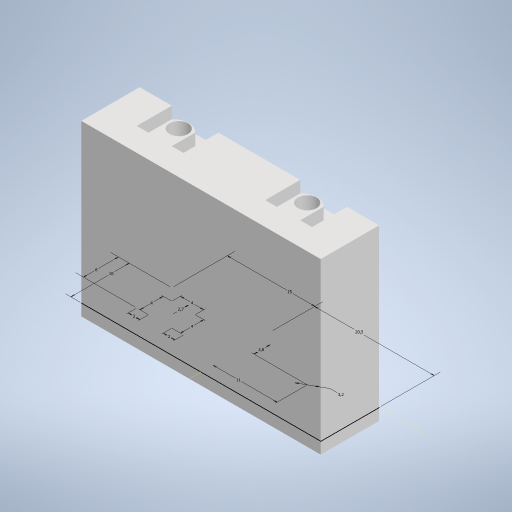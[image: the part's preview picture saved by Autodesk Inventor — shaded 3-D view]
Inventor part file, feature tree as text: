
AUTODESK INVENTOR PART (.ipt)
format: ipt  version: 2024.2 (Build 282272000, 272)  size: 267,264 bytes
history: native  units: mm
features: extrude x3, sketch x3, other x1
ambient origin geometry x8: Origin, YZ Plane, XZ Plane, XY Plane, X Axis, Y Axis, Z Axis, Center Point
bodies: Body1 (feature_tree)
feature tree (7):
  other  "Bryła1"
  extrude  "Wyciągnięcie proste1"  Depth=41.0mm
  sketch  "Szkic2"
  sketch  "Szkic3"
  extrude  "Wyciągnięcie proste2"  Depth=24.8mm
  extrude  "Wyciągnięcie proste3"  Depth=10.0mm TaperAngle=0.0deg
  sketch  "Szkic1"
